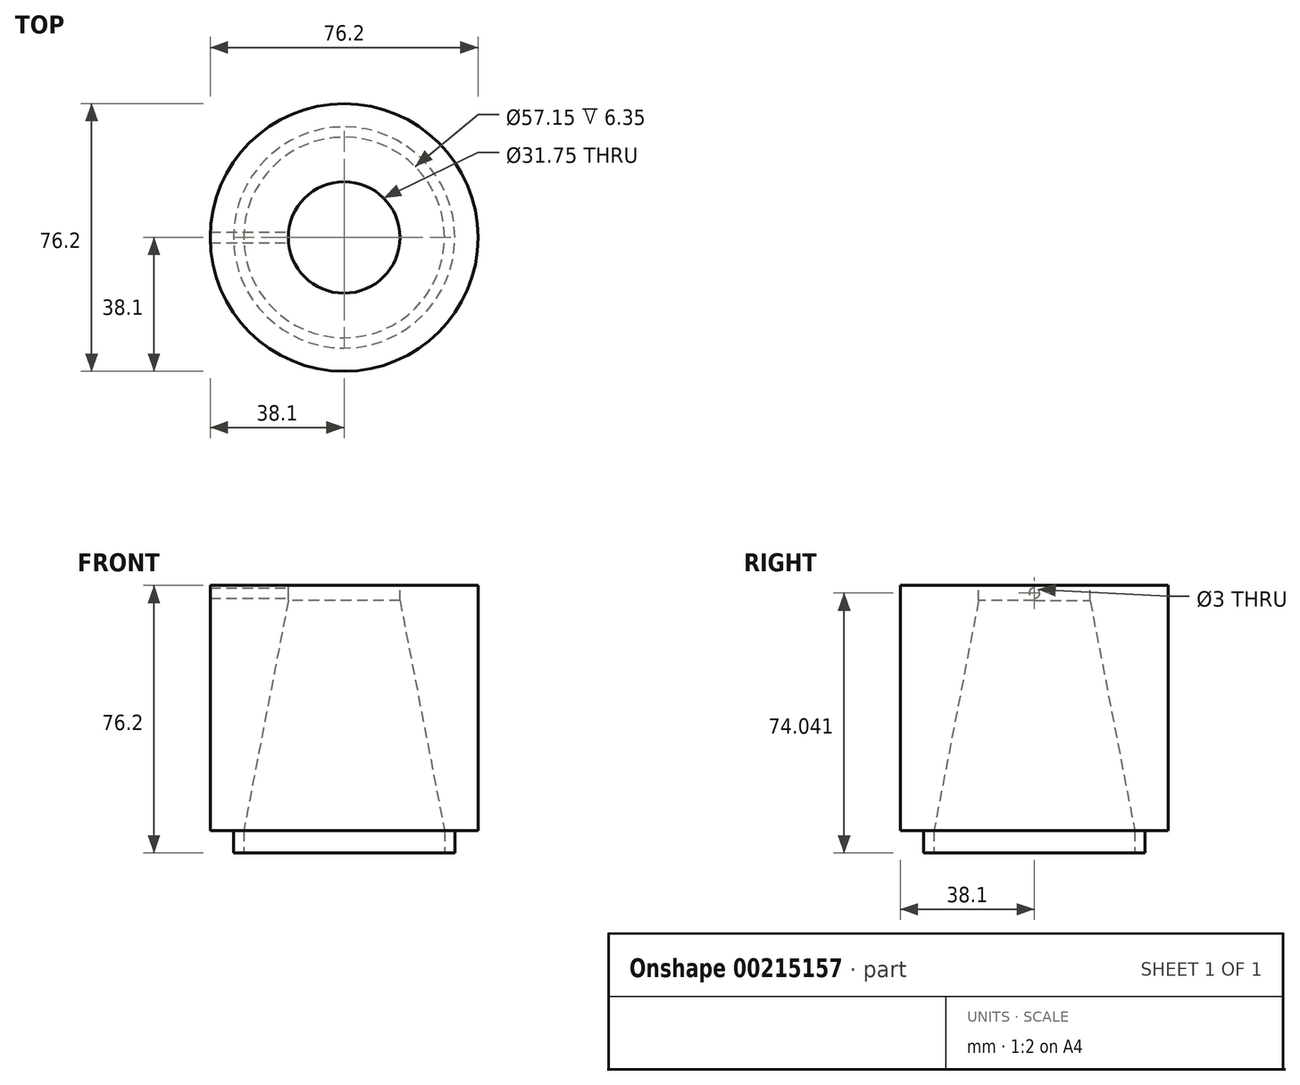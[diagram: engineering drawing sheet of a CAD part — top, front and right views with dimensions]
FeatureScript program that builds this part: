
annotation { "Feature Type Name" : "Feature", "Feature Type Description" : "" }
export const myFeature = defineFeature(function(context is Context, id is Id, definition is map)
    precondition{}
    {
        {
            var Q0;
            Q0=qCreatedBy(makeId("Top.planeOp"),FACE);
            var sketch = newSketch(context, id + "F0", { "sketchPlane" : qUnion([Q0])});
            skCircle(sketch, "E0", {"center": v(0, 0) * mm, "radius": 38.1 * mm});
            skSolve(sketch);
        }
        {
            var Q0;
            Q0 = qSketchRegion(id + "F0", true);
            extrude(context, id + "F1", {"entities" : qUnion([Q0]), "depth" : 76.2 * mm});
        }
        {
            var Q0;
            Q0=makeQuery(id+"F1.opExtrude","CAP_FACE",FACE,{"disambiguationData":[OSD([sQuery(id+"F0.wireOp",EDGE,"E0")])],"isStart":false});
            var sketch = newSketch(context, id + "F2", { "sketchPlane" : qUnion([Q0])});
            skCircle(sketch, "E1", {"center": v(0, 0) * mm, "radius": 15.88 * mm});
            skSolve(sketch);
        }
        {
            var Q0;
            Q0=makeQuery(id+"F1.opExtrude","CAP_FACE",FACE,{"disambiguationData":[OSD([sQuery(id+"F0.wireOp",EDGE,"E0")])],"isStart":true});
            var sketch = newSketch(context, id + "F3", { "sketchPlane" : qUnion([Q0])});
            skCircle(sketch, "E2", {"center": v(0, 0) * mm, "radius": 28.58 * mm});
            skSolve(sketch);
        }
        {
            var Q0;
            Q0 = qSketchRegion(id + "F3", true);
            extrude(context, id + "F4", {"entities" : qUnion([Q0]), "operationType" : NewBodyOperationType.REMOVE, "oppositeDirection" : true, "depth" : 6.35 * mm});
        }
        {
            var Q0;
            Q0=qCreatedBy(makeId("Right.planeOp"),FACE);
            var sketch = newSketch(context, id + "F5", { "sketchPlane" : qUnion([Q0])});
            skCircle(sketch, "E3", {"center": v(0, 74.04) * mm, "radius": 1.5 * mm});
            skSolve(sketch);
        }
        {
            var Q0;
            Q0 = qSketchRegion(id + "F5", true);
            extrude(context, id + "F6", {"entities" : qUnion([Q0]), "operationType" : NewBodyOperationType.REMOVE, "oppositeDirection" : true, "depth" : 50.8 * mm});
        }
        {
            var Q0;
            Q0=makeQuery(id+"F2.imprint","IMPRINT",FACE,{"disambiguationData":[TD([[makeQuery(id+"F2.imprint","IMPRINT",EDGE,{"derivedFrom":sQuery(id+"F2.wireOp",EDGE,"E1")}),1.0]])]});
            extrude(context, id + "F7", {"entities" : qUnion([Q0]), "operationType" : NewBodyOperationType.REMOVE, "oppositeDirection" : true, "depth" : 4.32 * mm});
        }
        {
            var Q1;
            Q1=makeQuery(id+"F7.boolean.opBoolean","COPY",FACE,{"derivedFrom":makeQuery(id+"F7.opExtrude","CAP_FACE",FACE,{"disambiguationData":[OSD([sQuery(id+"F2.wireOp",EDGE,"E1")])],"isStart":false})});
            var Q2;
            Q2=makeQuery(id+"F4.boolean.opBoolean","COPY",FACE,{"derivedFrom":makeQuery(id+"F4.opExtrude","CAP_FACE",FACE,{"disambiguationData":[OSD([sQuery(id+"F3.wireOp",EDGE,"E2")])],"isStart":false})});
            loft(context, id + "F8", {"operationType" : NewBodyOperationType.REMOVE, "sheetProfilesArray" : [{ "sheetProfileEntities" : qUnion([Q1]) }, { "sheetProfileEntities" : qUnion([Q2]) }]});
        }
        {
            var Q0;
            Q0=makeQuery(id+"F3.imprint","IMPRINT",FACE,{"disambiguationData":[TD([[makeQuery(id+"F3.imprint","IMPRINT",EDGE,{"derivedFrom":sQuery(id+"F3.wireOp",EDGE,"E2")}),-1.0]])]});
            var sketch = newSketch(context, id + "F9", { "sketchPlane" : qUnion([Q0])});
            skCircle(sketch, "E4", {"center": v(0, 0) * mm, "radius": 31.5 * mm});
            skCircle(sketch, "E5.0", {"center": v(0, 0) * mm, "radius": 38.1 * mm});
            skSolve(sketch);
        }
        {
            var Q0;
            Q0 = qSketchRegion(id + "F9", true);
            extrude(context, id + "F10", {"entities" : qUnion([Q0]), "operationType" : NewBodyOperationType.REMOVE, "oppositeDirection" : true, "depth" : 6.35 * mm});
        }
    });
